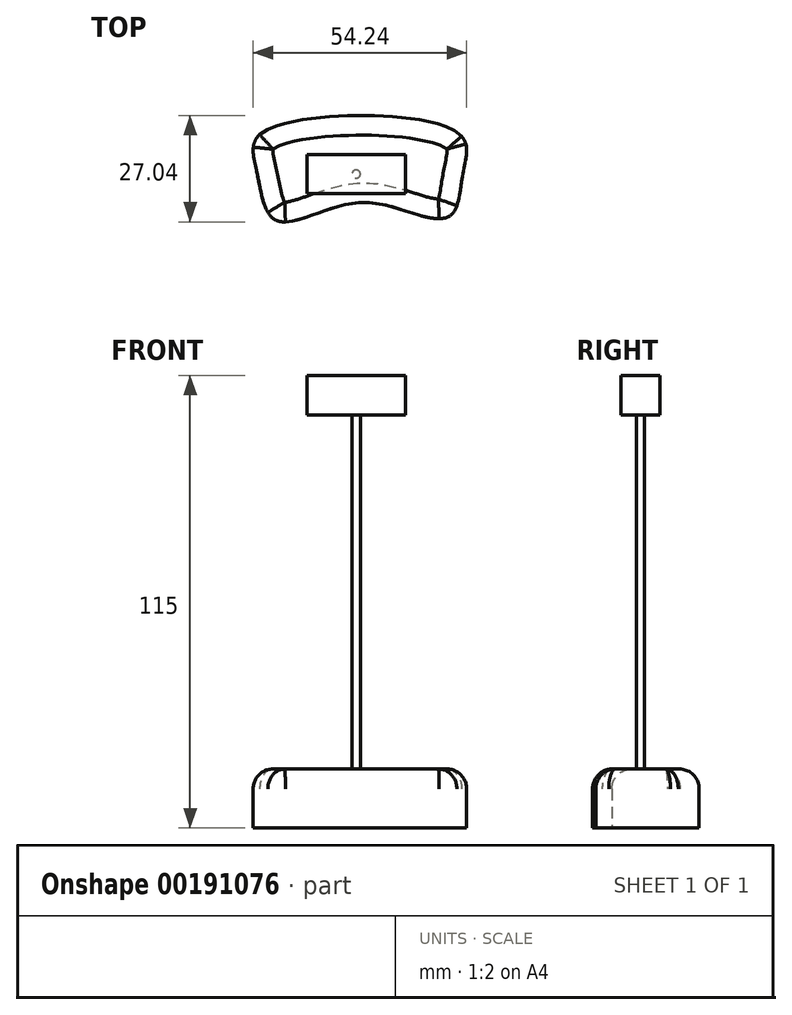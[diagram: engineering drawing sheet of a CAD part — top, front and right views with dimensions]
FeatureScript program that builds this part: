
annotation { "Feature Type Name" : "Feature", "Feature Type Description" : "" }
export const myFeature = defineFeature(function(context is Context, id is Id, definition is map)
    precondition{}
    {
        {
            var Q0;
            Q0=qCreatedBy(makeId("Front.planeOp"),FACE);
            var sketch = newSketch(context, id + "F0", { "sketchPlane" : qUnion([Q0])});
            skLineSegment(sketch, "E0.bottom", {"start": v(-59.87, 11.47) * mm, "end": v(-34.87, 11.47) * mm});
            skLineSegment(sketch, "E0.top", {"start": v(-59.87, 1.47) * mm, "end": v(-34.87, 1.47) * mm});
            skLineSegment(sketch, "E0.left", {"start": v(-59.87, 11.47) * mm, "end": v(-59.87, 1.47) * mm});
            skLineSegment(sketch, "E0.right", {"start": v(-34.87, 11.47) * mm, "end": v(-34.87, 1.47) * mm});
            skSolve(sketch);
        }
        {
            var Q0;
            Q0 = qSketchRegion(id + "F0", true);
            var Q1;
            Q1=makeQuery(id+"F0.imprint","IMPRINT",FACE,{"disambiguationData":[TD([[makeQuery(id+"F0.imprint","IMPRINT",EDGE,{"derivedFrom":sQuery(id+"F0.wireOp",EDGE,"E0.bottom")}),-1.0]])]});
            extrude(context, id + "F1", {"entities" : qUnion([Q0, Q1]), "depth" : 10 * mm});
        }
        {
            var Q0;
            Q0=makeQuery(id+"F1.opExtrude","SWEPT_FACE",FACE,{"disambiguationData":[OSD([sQuery(id+"F0.wireOp",EDGE,"E0.top")])]});
            var sketch = newSketch(context, id + "F2", { "sketchPlane" : qUnion([Q0])});
            skPoint(sketch, "E1", {"position": v(-47.37, 5) * mm});
            skPoint(sketch, "E1.positionSnap0", {"position": v(-59.87, 5) * mm});
            skPoint(sketch, "E1.positionSnap1", {"position": v(-47.37, 10) * mm});
            skCircle(sketch, "E2", {"center": v(-47.37, 5) * mm, "radius": 1.05 * mm});
            skSolve(sketch);
        }
        {
            var Q0;
            Q0 = qSketchRegion(id + "F2", true);
            extrude(context, id + "F3", {"entities" : qUnion([Q0]), "operationType" : NewBodyOperationType.ADD, "depth" : 90 * mm});
        }
        {
            var Q0;
            Q0=makeQuery(id+"F3.opExtrude","CAP_FACE",FACE,{"disambiguationData":[OSD([sQuery(id+"F2.wireOp",EDGE,"E2")])],"isStart":false});
            var sketch = newSketch(context, id + "F4", { "sketchPlane" : qUnion([Q0])});
            skFitSpline(sketch, "E3", {"points": [v(-72.55, 4.68) * mm, v(-67.6, 16.8) * mm, v(-48.05, 12.4) * mm, v(-30.43, 15.7) * mm, v(-23, 15.14) * mm, v(-20.24, 4.96) * mm, v(-21.9, -5.78) * mm, v(-70.9, -5.78) * mm, v(-72.55, 4.68) * mm]});
            skSolve(sketch);
        }
        {
            var Q0;
            Q0 = qSketchRegion(id + "F4", true);
            extrude(context, id + "F5", {"entities" : qUnion([Q0]), "operationType" : NewBodyOperationType.ADD, "depth" : 15 * mm});
        }
        {
            var Q0;
            Q0=makeQuery(id+"F5.opExtrude","CAP_EDGE",EDGE,{"disambiguationData":[OSD([sQuery(id+"F4.wireOp",EDGE,"E3")])],"isStart":true});
            fillet(context, id + "F6", {"entities" : qUnion([Q0]), "radius" : 5 * mm, "tangentPropagation" : true, "allowEdgeOverflow" : false});
        }
    });
